# Revit family: QF_ELECTROLUXPROFESSIONAL_1LSNTF_WS6-20_S
name_source: partatom
category: Attrezzature speciali
units: mm (PartAtom-declared; Revit-internal decimal feet)

## family parameters
Basato su piano di lavoro = No
Condiviso = No
Punto di calcolo locali = No
Quota connettore circolare = Usa diametro
Sempre verticale = Sì
Taglio con vuoti quando caricato = No
Tipo di parte = Normale

## types (1)
- 9867830199
    Cycle = 50 Hz
    Depth = 915.5 mm  [stored 3.00361 ft]
    Depth Actual = 915 mm  [stored 3.00197 ft]
    Descrizione = WASHER WS6-20 20KG STEAM 220-230/50/1N COMPASS PRO 6G01 CH-EN 2xWATER POWDER+5xLIQ. VALV.OPEN SILVER 2.I/O DISCON. STOP
    Gas KW = 0
    Height = 1346.8 mm  [stored 4.41864 ft]
    Height Actual = 1345 mm
    Item Number = 1LD05P
    Latent Heat Output = 0.0
    Length Actual = 750 mm  [stored 2.46063 ft]
    Modello = WS6-20
    Phase = 1
    Produttore = Electrolux Professional
    Prospetto di default = 0 mm  [stored 0 ft]
    Sensible Heat Output = 0.0
    Steam Pounds per Hour = 0
    URL = www.electroluxprofessional.com
    Volts = 240 V
    Watts = 800 W
    Weight = 221
    Width = 750 mm  [stored 2.46063 ft]

note: [stored X ft] marks values corroborated as IEEE doubles in the binary element streams (Revit-internal decimal feet)

## geometry (parser evidence)
native form markers: Sweep x4
no freeform markers — native parametric forms only
